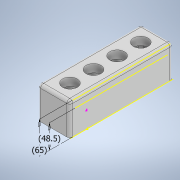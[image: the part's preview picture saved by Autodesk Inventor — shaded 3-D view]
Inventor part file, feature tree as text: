
AUTODESK INVENTOR PART (.ipt)
format: ipt  version: 2021 (Build 250183000, 183)  size: 204,288 bytes
history: native  units: in
note: dims shown in document units (in); Inventor stores cm internally (conversion verified against a paired STEP export)
features: extrude x4, sketch x3, fillet x3, other x2, imported_body x1
ambient origin geometry x8: Origin, YZ Plane, XZ Plane, XY Plane, X Axis, Y Axis, Z Axis, Center Point
bodies: Body1 (feature_tree)
feature tree (13):
  extrude  "Extrusion2"  Depth=2.5591in
  extrude  "Extrusion3"  Depth=2.5591in
  extrude  "Extrusion4"  Depth=0.0591in
  sketch  "Sketch6"  dims[d6=8.2677in d7=2.5591in]
  fillet  "Fillet1"  Radius=1.3386in
  extrude  "Extrusion5"  Depth=0.0591in
  fillet  "Fillet2"  Radius=1.8898in
  sketch  "Sketch8"  dims[d11=1.3386in d12=1.3386in d13=1.3386in d14=1.8898in d15=1.8898in d16=1.8898in d19=0.7087in d20=0.0in d21=0.4331in d22=0.4331in d23=0.4331in d24=0.4331in d25=1.9094in d26=0.0in d27=1.1811in d28=1.1811in d29=1.1811in d30=1.1811in d31=0.9449in d32=4.1339in d33=1.6929in d34=1.9094in d35=1.2992in d36=0.2362in d38=0.3937in d39=0.0in d40=0.5in d41=0.2362in d42=2.5591in d43=0.0591in]
  fillet  "Fillet3"  Radius=1.8898in
  imported_body  "Base"
  other  "Top"
  other  "Walls"
  sketch  "Sketch7"  dims[d8=2.5591in d9=0.0in d10=1.3386in]
